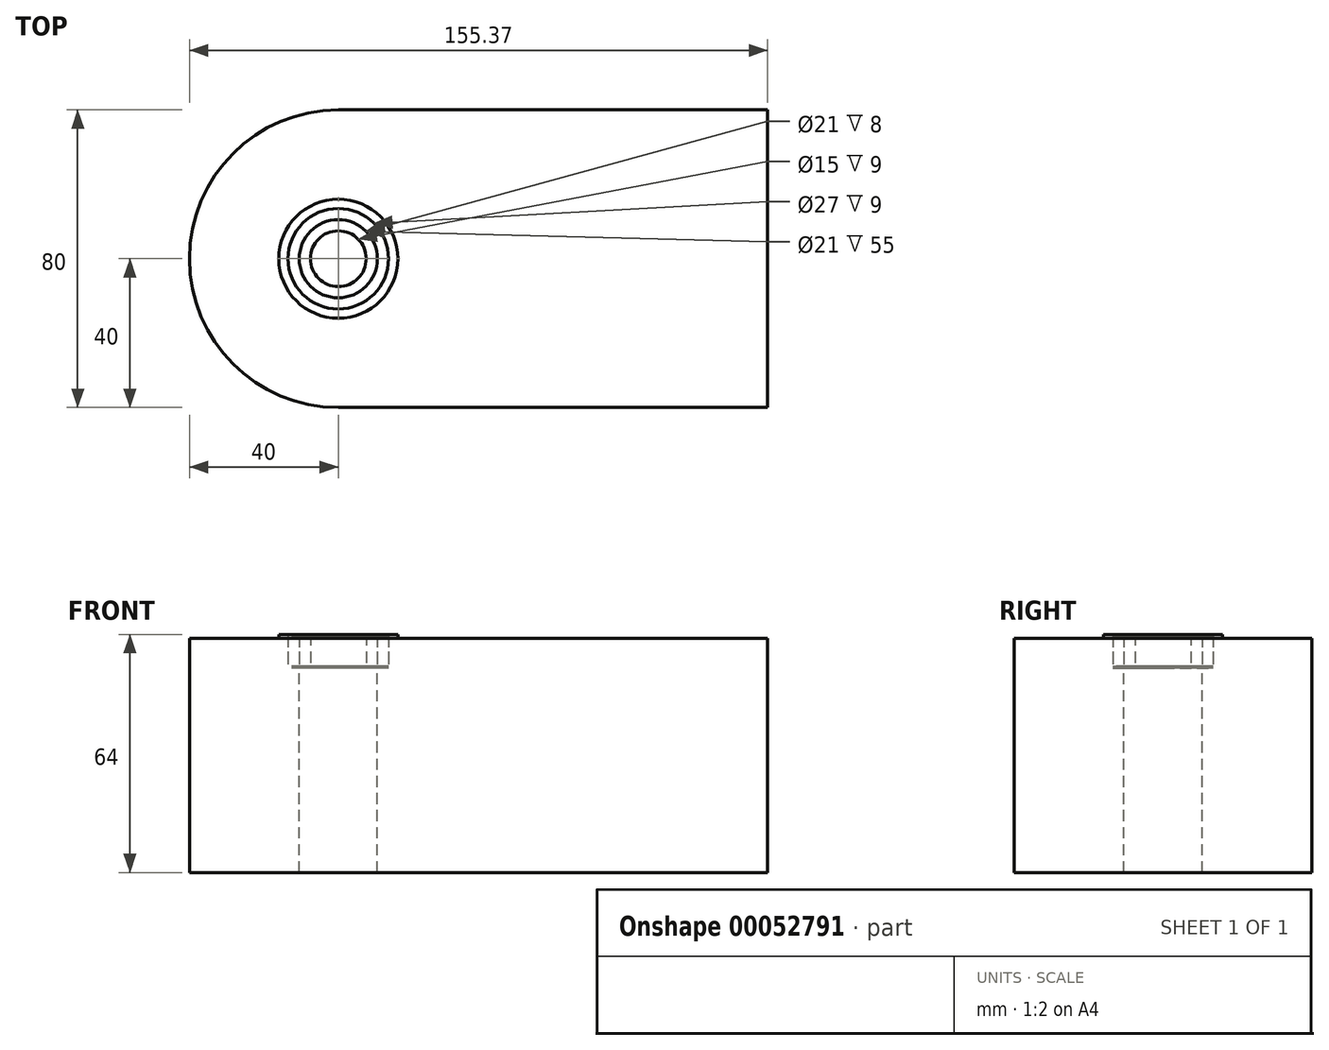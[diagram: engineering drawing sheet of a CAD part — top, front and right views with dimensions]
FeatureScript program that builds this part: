
annotation { "Feature Type Name" : "Feature", "Feature Type Description" : "" }
export const myFeature = defineFeature(function(context is Context, id is Id, definition is map)
    precondition{}
    {
        {
            var Q0;
            Q0=qCreatedBy(makeId("Top.planeOp"),FACE);
            var sketch = newSketch(context, id + "F0", { "sketchPlane" : qUnion([Q0])});
            skCircle(sketch, "E0", {"center": v(0, 0) * mm, "radius": 7.5 * mm});
            skCircle(sketch, "E1", {"center": v(0, 0) * mm, "radius": 16 * mm});
            skCircle(sketch, "E2", {"center": v(0, 0) * mm, "radius": 10.5 * mm});
            skCircle(sketch, "E3", {"center": v(0, 0) * mm, "radius": 13.5 * mm});
            skSolve(sketch);
        }
        {
            var Q0;
            Q0=makeQuery(id+"F0.imprint","IMPRINT",FACE,{"disambiguationData":[TD([[makeQuery(id+"F0.imprint","IMPRINT",EDGE,{"derivedFrom":sQuery(id+"F0.wireOp",EDGE,"E1")}),1.0]])]});
            var Q1;
            Q1=makeQuery(id+"F0.imprint","IMPRINT",FACE,{"disambiguationData":[TD([[makeQuery(id+"F0.imprint","IMPRINT",EDGE,{"derivedFrom":sQuery(id+"F0.wireOp",EDGE,"E0")}),-1.0]])]});
            extrude(context, id + "F1", {"entities" : qUnion([Q0, Q1]), "depth" : 9 * mm});
        }
        {
            var Q0;
            Q0=makeQuery(id+"F0.imprint","IMPRINT",FACE,{"disambiguationData":[TD([[makeQuery(id+"F0.imprint","IMPRINT",EDGE,{"derivedFrom":sQuery(id+"F0.wireOp",EDGE,"E2")}),-1.0]])]});
            extrude(context, id + "F2", {"entities" : qUnion([Q0]), "depth" : 8.5 * mm});
        }
        {
            var Q0;
            Q0=makeQuery(id+"F2.opExtrude","CAP_FACE",FACE,{"disambiguationData":[OSD([sQuery(id+"F0.wireOp",EDGE,"E2"),sQuery(id+"F0.wireOp",EDGE,"E3")])],"isStart":true});
            extrude(context, id + "F3", {"entities" : qUnion([Q0]), "operationType" : NewBodyOperationType.REMOVE, "oppositeDirection" : true, "depth" : 0.5 * mm});
        }
        {
            var Q0;
            Q0=qCreatedBy(makeId("Top.planeOp"),FACE);
            var sketch = newSketch(context, id + "F4", { "sketchPlane" : qUnion([Q0])});
            skArc(sketch, "E4", {"start": v(0, 40) * mm, "mid": v(-40, 0) * mm, "end": v(0, -40) * mm});
            skLineSegment(sketch, "E5", {"start": v(0, 40) * mm, "end": v(115.37, 40) * mm});
            skLineSegment(sketch, "E6", {"start": v(0, -40) * mm, "end": v(115.37, -40) * mm});
            skLineSegment(sketch, "E7", {"start": v(115.37, -40) * mm, "end": v(115.37, 40) * mm});
            skCircle(sketch, "E8", {"center": v(0, 0) * mm, "radius": 16 * mm});
            skCircle(sketch, "E9", {"center": v(0, 0) * mm, "radius": 10.5 * mm});
            skSolve(sketch);
        }
        {
            var Q0;
            Q0=makeQuery(id+"F4.imprint","IMPRINT",FACE,{"disambiguationData":[TD([[makeQuery(id+"F4.imprint","IMPRINT",EDGE,{"derivedFrom":sQuery(id+"F4.wireOp",EDGE,"E4")}),1.0]])]});
            extrude(context, id + "F5", {"entities" : qUnion([Q0]), "depth" : 8 * mm});
        }
        {
            var Q0;
            Q0=makeQuery(id+"F4.imprint","IMPRINT",FACE,{"disambiguationData":[TD([[makeQuery(id+"F4.imprint","IMPRINT",EDGE,{"derivedFrom":sQuery(id+"F4.wireOp",EDGE,"E8")}),1.0]])]});
            var Q1;
            Q1=makeQuery(id+"F4.imprint","IMPRINT",FACE,{"disambiguationData":[TD([[makeQuery(id+"F4.imprint","IMPRINT",EDGE,{"derivedFrom":sQuery(id+"F4.wireOp",EDGE,"E4")}),1.0]])]});
            extrude(context, id + "F6", {"entities" : qUnion([Q0, Q1]), "operationType" : NewBodyOperationType.ADD, "oppositeDirection" : true, "depth" : 55 * mm});
        }
    });
